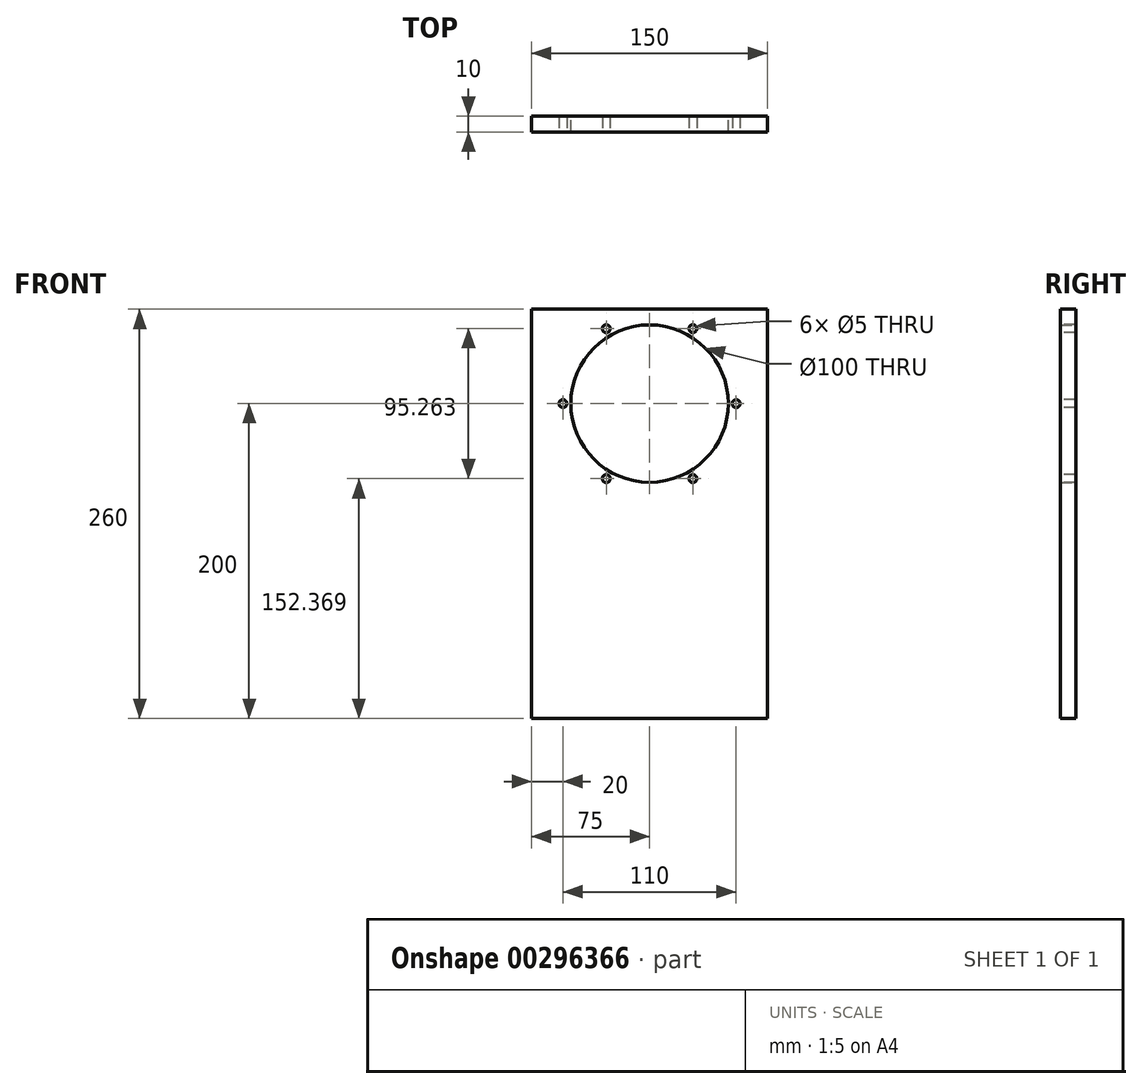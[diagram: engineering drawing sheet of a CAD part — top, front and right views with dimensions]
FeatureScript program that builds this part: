
annotation { "Feature Type Name" : "Feature", "Feature Type Description" : "" }
export const myFeature = defineFeature(function(context is Context, id is Id, definition is map)
    precondition{}
    {
        {
            var Q0;
            Q0=qCreatedBy(makeId("Front.planeOp"),FACE);
            var sketch = newSketch(context, id + "F0", { "sketchPlane" : qUnion([Q0])});
            skLineSegment(sketch, "E0", {"start": v(0, 0) * mm, "end": v(0, 400) * mm, "construction": true});
            skLineSegment(sketch, "E1.bottom", {"start": v(-75, 260) * mm, "end": v(75, 260) * mm});
            skLineSegment(sketch, "E1.top", {"start": v(-75, 0) * mm, "end": v(75, 0) * mm});
            skLineSegment(sketch, "E1.left", {"start": v(-75, 260) * mm, "end": v(-75, 0) * mm});
            skLineSegment(sketch, "E1.right", {"start": v(75, 260) * mm, "end": v(75, 0) * mm});
            skCircle(sketch, "E2", {"center": v(0, 200) * mm, "radius": 50 * mm});
            skSolve(sketch);
        }
        {
            var Q0;
            Q0 = qSketchRegion(id + "F0", true);
            extrude(context, id + "F1", {"entities" : qUnion([Q0]), "depth" : 10 * mm});
        }
        {
            var Q0;
            Q0=makeQuery(id+"F1.opExtrude","CAP_FACE",FACE,{"disambiguationData":[OSD([sQuery(id+"F0.wireOp",EDGE,"E1.bottom"),sQuery(id+"F0.wireOp",EDGE,"E1.top"),sQuery(id+"F0.wireOp",EDGE,"E1.left"),sQuery(id+"F0.wireOp",EDGE,"E1.right"),sQuery(id+"F0.wireOp",EDGE,"E2")])],"isStart":false});
            var sketch = newSketch(context, id + "F2", { "sketchPlane" : qUnion([Q0])});
            skCircle(sketch, "E3.cCircle", {"center": v(0, 200) * mm, "radius": 47.63 * mm, "construction": true});
            skLineSegment(sketch, "E3.0", {"start": v(27.5, 247.63) * mm, "end": v(55, 200) * mm});
            skLineSegment(sketch, "E3.1", {"start": v(55, 200) * mm, "end": v(27.5, 152.37) * mm});
            skLineSegment(sketch, "E3.2", {"start": v(27.5, 152.37) * mm, "end": v(-27.5, 152.37) * mm});
            skLineSegment(sketch, "E3.3", {"start": v(-27.5, 152.37) * mm, "end": v(-55, 200) * mm});
            skLineSegment(sketch, "E3.4", {"start": v(-55, 200) * mm, "end": v(-27.5, 247.63) * mm});
            skLineSegment(sketch, "E3.5", {"start": v(-27.5, 247.63) * mm, "end": v(27.5, 247.63) * mm});
            skPoint(sketch, "E3.0.midPoint", {"position": v(41.25, 223.82) * mm});
            skPoint(sketch, "E4", {"position": v(-27.5, 247.63) * mm});
            skPoint(sketch, "E5", {"position": v(27.5, 247.63) * mm});
            skPoint(sketch, "E6", {"position": v(55, 200) * mm});
            skPoint(sketch, "E7", {"position": v(27.5, 152.37) * mm});
            skPoint(sketch, "E8", {"position": v(-27.5, 152.37) * mm});
            skPoint(sketch, "E9", {"position": v(-55, 200) * mm});
            skSolve(sketch);
        }
        {
            var Q0;
            Q0=sQuery(id+"F2.wireOp",VERTEX,"E4");
            var Q1;
            Q1=sQuery(id+"F2.wireOp",VERTEX,"E5");
            var Q2;
            Q2=sQuery(id+"F2.wireOp",VERTEX,"E6");
            var Q3;
            Q3=sQuery(id+"F2.wireOp",VERTEX,"E7");
            var Q4;
            Q4=sQuery(id+"F2.wireOp",VERTEX,"E8");
            var Q5;
            Q5=sQuery(id+"F2.wireOp",VERTEX,"E9");
            var Q6;
            Q6=makeQuery(id+"F1.opExtrude","SWEPT_BODY",BODY,{"disambiguationData":[OSD([sQuery(id+"F0.wireOp",EDGE,"E1.bottom"),sQuery(id+"F0.wireOp",EDGE,"E1.top"),sQuery(id+"F0.wireOp",EDGE,"E1.left"),sQuery(id+"F0.wireOp",EDGE,"E1.right"),sQuery(id+"F0.wireOp",EDGE,"E2")])]});
            hole(context, id + "F3", {"style" : HoleStyle.SIMPLE, "endStyle" : HoleEndStyle.THROUGH, "standardTappedOrClearance" : lookupTablePath({ "standard" : "ISO", "engagement" : "75%", "pitch" : "1 mm", "size" : "M6", "type" : "Tapped" }), "standardBlindInLast" : lookupTablePath({ "standard" : "ISO", "engagement" : "75%", "pitch" : "1 mm", "size" : "M6", "type" : "Tapped" }), "holeDiameter" : 5 * mm, "showTappedDepth" : true, "tappedDepth" : 9.6 * mm, "tapClearance" : 3, "locations" : qUnion([Q0, Q1, Q2, Q3, Q4, Q5]), "scope" : qUnion([Q6]), "majorDiameter" : 6 * mm});
        }
    });
